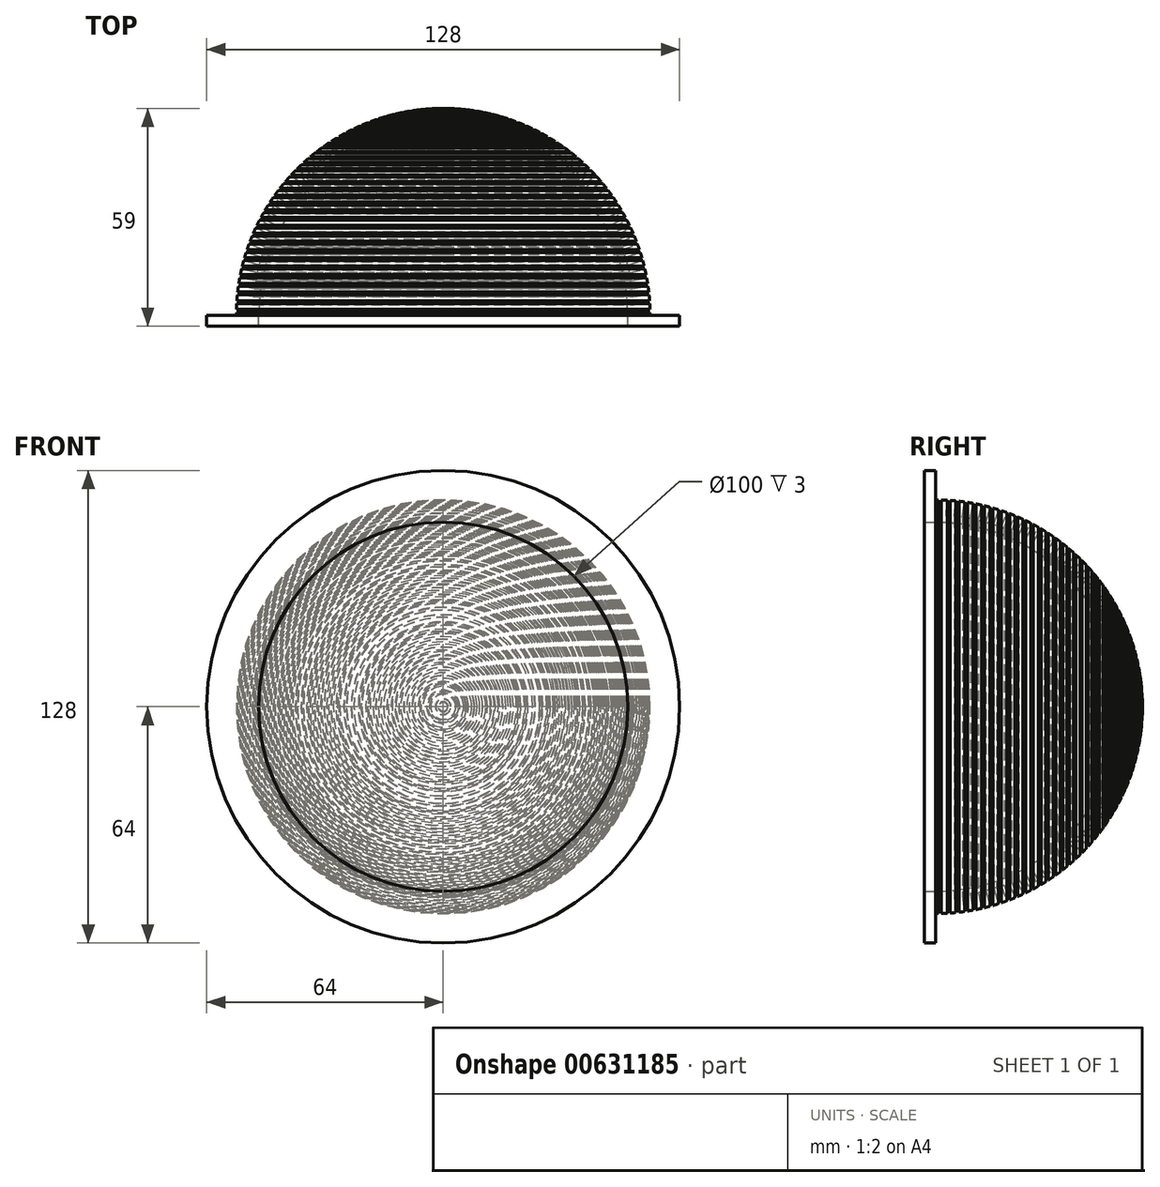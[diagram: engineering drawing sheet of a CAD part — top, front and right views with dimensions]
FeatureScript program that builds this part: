
annotation { "Feature Type Name" : "Feature", "Feature Type Description" : "" }
export const myFeature = defineFeature(function(context is Context, id is Id, definition is map)
    precondition{}
    {
        {
            var Q0;
            Q0=qCreatedBy(makeId("Right.planeOp"),FACE);
            var sketch = newSketch(context, id + "F0", { "sketchPlane" : qUnion([Q0])});
            skArc(sketch, "E0", {"start": v(0, 50) * mm, "mid": v(50, 0) * mm, "end": v(0, -50) * mm});
            skArc(sketch, "E1", {"start": v(0, 56) * mm, "mid": v(56, 0) * mm, "end": v(0, -56) * mm});
            skLineSegment(sketch, "E2", {"start": v(0, 50) * mm, "end": v(0, 56) * mm});
            skLineSegment(sketch, "E3", {"start": v(0, -50) * mm, "end": v(0, -56) * mm});
            skPoint(sketch, "E4", {"position": v(56, 0) * mm});
            skPoint(sketch, "E5", {"position": v(0, 56) * mm});
            skArc(sketch, "E6", {"start": v(0, 51.7) * mm, "mid": v(36.56, 36.56) * mm, "end": v(51.7, 0) * mm, "construction": true});
            skPoint(sketch, "E7", {"position": v(1.1, 51.69) * mm});
            skLineSegment(sketch, "E8", {"start": v(1.1, 51.69) * mm, "end": v(0.7, 51.7) * mm});
            skLineSegment(sketch, "E9", {"start": v(0.7, 51.7) * mm, "end": v(0.83, 57.63) * mm});
            skLineSegment(sketch, "E10", {"start": v(0.83, 57.63) * mm, "end": v(1.63, 57.62) * mm});
            skLineSegment(sketch, "E11", {"start": v(1.63, 57.62) * mm, "end": v(1.5, 51.68) * mm});
            skLineSegment(sketch, "E12", {"start": v(1.5, 51.68) * mm, "end": v(1.1, 51.69) * mm});
            skLineSegment(sketch, "E13.1.0", {"start": v(2.88, 51.62) * mm, "end": v(3.26, 57.55) * mm});
            skPoint(sketch, "E13.1.1", {"position": v(3.28, 51.6) * mm});
            skPoint(sketch, "E13.1.2", {"position": v(2.36, 55.95) * mm});
            skLineSegment(sketch, "E13.1.3", {"start": v(4.05, 57.5) * mm, "end": v(3.68, 51.57) * mm});
            skLineSegment(sketch, "E13.1.4", {"start": v(3.26, 57.55) * mm, "end": v(4.05, 57.5) * mm});
            skLineSegment(sketch, "E13.1.5", {"start": v(3.28, 51.6) * mm, "end": v(2.88, 51.62) * mm});
            skLineSegment(sketch, "E13.1.6", {"start": v(3.68, 51.57) * mm, "end": v(3.28, 51.6) * mm});
            skLineSegment(sketch, "E13.2.0", {"start": v(5.05, 51.45) * mm, "end": v(5.68, 57.36) * mm});
            skPoint(sketch, "E13.2.1", {"position": v(5.45, 51.41) * mm});
            skPoint(sketch, "E13.2.2", {"position": v(4.72, 55.8) * mm});
            skLineSegment(sketch, "E13.2.3", {"start": v(6.48, 57.27) * mm, "end": v(5.85, 51.37) * mm});
            skLineSegment(sketch, "E13.2.4", {"start": v(5.68, 57.36) * mm, "end": v(6.48, 57.27) * mm});
            skLineSegment(sketch, "E13.2.5", {"start": v(5.45, 51.41) * mm, "end": v(5.05, 51.45) * mm});
            skLineSegment(sketch, "E13.2.6", {"start": v(5.85, 51.37) * mm, "end": v(5.45, 51.41) * mm});
            skLineSegment(sketch, "E13.anchor1", {"start": v(0, 0) * mm, "end": v(0.7, 51.7) * mm, "construction": true});
            skLineSegment(sketch, "E13.anchor2", {"start": v(0, 0) * mm, "end": v(51.66, 2) * mm, "construction": true});
            skLineSegment(sketch, "E14.1.3.0", {"start": v(7.22, 51.2) * mm, "end": v(8.1, 57.07) * mm});
            skPoint(sketch, "E14.3.3.0", {"position": v(7.61, 51.14) * mm});
            skPoint(sketch, "E14.4.3.0", {"position": v(7.07, 55.55) * mm});
            skLineSegment(sketch, "E14.5.3.0", {"start": v(8.88, 56.95) * mm, "end": v(8, 51.08) * mm});
            skLineSegment(sketch, "E14.8.3.0", {"start": v(8.1, 57.07) * mm, "end": v(8.88, 56.95) * mm});
            skLineSegment(sketch, "E14.11.3.0", {"start": v(7.61, 51.14) * mm, "end": v(7.22, 51.2) * mm});
            skLineSegment(sketch, "E14.14.3.0", {"start": v(8, 51.08) * mm, "end": v(7.61, 51.14) * mm});
            skLineSegment(sketch, "E14.1.4.0", {"start": v(9.37, 50.85) * mm, "end": v(10.5, 56.68) * mm});
            skPoint(sketch, "E14.3.4.0", {"position": v(9.76, 50.77) * mm});
            skPoint(sketch, "E14.4.4.0", {"position": v(9.4, 55.2) * mm});
            skLineSegment(sketch, "E14.5.4.0", {"start": v(11.28, 56.53) * mm, "end": v(10.16, 50.7) * mm});
            skLineSegment(sketch, "E14.8.4.0", {"start": v(10.5, 56.68) * mm, "end": v(11.28, 56.53) * mm});
            skLineSegment(sketch, "E14.11.4.0", {"start": v(9.76, 50.77) * mm, "end": v(9.37, 50.85) * mm});
            skLineSegment(sketch, "E14.14.4.0", {"start": v(10.16, 50.7) * mm, "end": v(9.76, 50.77) * mm});
            skLineSegment(sketch, "E14.1.5.0", {"start": v(11.5, 50.4) * mm, "end": v(12.87, 56.18) * mm});
            skPoint(sketch, "E14.3.5.0", {"position": v(11.9, 50.31) * mm});
            skPoint(sketch, "E14.4.5.0", {"position": v(11.72, 54.76) * mm});
            skLineSegment(sketch, "E14.5.5.0", {"start": v(13.65, 56) * mm, "end": v(12.28, 50.22) * mm});
            skLineSegment(sketch, "E14.8.5.0", {"start": v(12.87, 56.18) * mm, "end": v(13.65, 56) * mm});
            skLineSegment(sketch, "E14.11.5.0", {"start": v(11.9, 50.31) * mm, "end": v(11.5, 50.4) * mm});
            skLineSegment(sketch, "E14.14.5.0", {"start": v(12.28, 50.22) * mm, "end": v(11.9, 50.31) * mm});
            skLineSegment(sketch, "E14.1.6.0", {"start": v(13.62, 49.87) * mm, "end": v(15.23, 55.6) * mm});
            skPoint(sketch, "E14.3.6.0", {"position": v(14, 49.77) * mm});
            skPoint(sketch, "E14.4.6.0", {"position": v(14.02, 54.22) * mm});
            skLineSegment(sketch, "E14.5.6.0", {"start": v(16, 55.37) * mm, "end": v(14.4, 49.66) * mm});
            skLineSegment(sketch, "E14.8.6.0", {"start": v(15.23, 55.6) * mm, "end": v(16, 55.37) * mm});
            skLineSegment(sketch, "E14.11.6.0", {"start": v(14, 49.77) * mm, "end": v(13.62, 49.87) * mm});
            skLineSegment(sketch, "E14.14.6.0", {"start": v(14.4, 49.66) * mm, "end": v(14, 49.77) * mm});
            skLineSegment(sketch, "E14.1.7.0", {"start": v(15.71, 49.26) * mm, "end": v(17.56, 54.9) * mm});
            skPoint(sketch, "E14.3.7.0", {"position": v(16.1, 49.13) * mm});
            skPoint(sketch, "E14.4.7.0", {"position": v(16.3, 53.58) * mm});
            skLineSegment(sketch, "E14.5.7.0", {"start": v(18.32, 54.65) * mm, "end": v(16.47, 49) * mm});
            skLineSegment(sketch, "E14.8.7.0", {"start": v(17.56, 54.9) * mm, "end": v(18.32, 54.65) * mm});
            skLineSegment(sketch, "E14.11.7.0", {"start": v(16.1, 49.13) * mm, "end": v(15.71, 49.26) * mm});
            skLineSegment(sketch, "E14.14.7.0", {"start": v(16.47, 49) * mm, "end": v(16.1, 49.13) * mm});
            skLineSegment(sketch, "E14.1.8.0", {"start": v(17.78, 48.55) * mm, "end": v(19.86, 54.11) * mm});
            skPoint(sketch, "E14.3.8.0", {"position": v(18.15, 48.4) * mm});
            skPoint(sketch, "E14.4.8.0", {"position": v(18.54, 52.84) * mm});
            skLineSegment(sketch, "E14.5.8.0", {"start": v(20.6, 53.83) * mm, "end": v(18.52, 48.27) * mm});
            skLineSegment(sketch, "E14.8.8.0", {"start": v(19.86, 54.11) * mm, "end": v(20.6, 53.83) * mm});
            skLineSegment(sketch, "E14.11.8.0", {"start": v(18.15, 48.4) * mm, "end": v(17.78, 48.55) * mm});
            skLineSegment(sketch, "E14.14.8.0", {"start": v(18.52, 48.27) * mm, "end": v(18.15, 48.4) * mm});
            skLineSegment(sketch, "E14.1.9.0", {"start": v(19.8, 47.76) * mm, "end": v(22.12, 53.22) * mm});
            skPoint(sketch, "E14.3.9.0", {"position": v(20.18, 47.6) * mm});
            skPoint(sketch, "E14.4.9.0", {"position": v(20.75, 52.01) * mm});
            skLineSegment(sketch, "E14.5.9.0", {"start": v(22.86, 52.91) * mm, "end": v(20.54, 47.44) * mm});
            skLineSegment(sketch, "E14.8.9.0", {"start": v(22.12, 53.22) * mm, "end": v(22.86, 52.91) * mm});
            skLineSegment(sketch, "E14.11.9.0", {"start": v(20.18, 47.6) * mm, "end": v(19.8, 47.76) * mm});
            skLineSegment(sketch, "E14.14.9.0", {"start": v(20.54, 47.44) * mm, "end": v(20.18, 47.6) * mm});
            skLineSegment(sketch, "E14.1.10.0", {"start": v(21.8, 46.88) * mm, "end": v(24.35, 52.24) * mm});
            skPoint(sketch, "E14.3.10.0", {"position": v(22.16, 46.7) * mm});
            skPoint(sketch, "E14.4.10.0", {"position": v(22.93, 51.1) * mm});
            skLineSegment(sketch, "E14.5.10.0", {"start": v(25.07, 51.9) * mm, "end": v(22.53, 46.54) * mm});
            skLineSegment(sketch, "E14.8.10.0", {"start": v(24.35, 52.24) * mm, "end": v(25.07, 51.9) * mm});
            skLineSegment(sketch, "E14.11.10.0", {"start": v(22.16, 46.7) * mm, "end": v(21.8, 46.88) * mm});
            skLineSegment(sketch, "E14.14.10.0", {"start": v(22.53, 46.54) * mm, "end": v(22.16, 46.7) * mm});
            skLineSegment(sketch, "E14.1.11.0", {"start": v(23.76, 45.92) * mm, "end": v(26.53, 51.17) * mm});
            skPoint(sketch, "E14.3.11.0", {"position": v(24.11, 45.73) * mm});
            skPoint(sketch, "E14.4.11.0", {"position": v(25.06, 50.08) * mm});
            skLineSegment(sketch, "E14.5.11.0", {"start": v(27.24, 50.8) * mm, "end": v(24.47, 45.55) * mm});
            skLineSegment(sketch, "E14.8.11.0", {"start": v(26.53, 51.17) * mm, "end": v(27.24, 50.8) * mm});
            skLineSegment(sketch, "E14.11.11.0", {"start": v(24.11, 45.73) * mm, "end": v(23.76, 45.92) * mm});
            skLineSegment(sketch, "E14.14.11.0", {"start": v(24.47, 45.55) * mm, "end": v(24.11, 45.73) * mm});
            skLineSegment(sketch, "E14.1.12.0", {"start": v(25.68, 44.88) * mm, "end": v(28.66, 50) * mm});
            skPoint(sketch, "E14.3.12.0", {"position": v(26.02, 44.67) * mm});
            skPoint(sketch, "E14.4.12.0", {"position": v(27.15, 48.98) * mm});
            skLineSegment(sketch, "E14.5.12.0", {"start": v(29.36, 49.6) * mm, "end": v(26.37, 44.47) * mm});
            skLineSegment(sketch, "E14.8.12.0", {"start": v(28.66, 50) * mm, "end": v(29.36, 49.6) * mm});
            skLineSegment(sketch, "E14.11.12.0", {"start": v(26.02, 44.67) * mm, "end": v(25.68, 44.88) * mm});
            skLineSegment(sketch, "E14.14.12.0", {"start": v(26.37, 44.47) * mm, "end": v(26.02, 44.67) * mm});
            skLineSegment(sketch, "E14.1.13.0", {"start": v(27.54, 43.75) * mm, "end": v(30.75, 48.75) * mm});
            skPoint(sketch, "E14.3.13.0", {"position": v(27.88, 43.54) * mm});
            skPoint(sketch, "E14.4.13.0", {"position": v(29.2, 47.8) * mm});
            skLineSegment(sketch, "E14.5.13.0", {"start": v(31.42, 48.32) * mm, "end": v(28.22, 43.32) * mm});
            skLineSegment(sketch, "E14.8.13.0", {"start": v(30.75, 48.75) * mm, "end": v(31.42, 48.32) * mm});
            skLineSegment(sketch, "E14.11.13.0", {"start": v(27.88, 43.54) * mm, "end": v(27.54, 43.75) * mm});
            skLineSegment(sketch, "E14.14.13.0", {"start": v(28.22, 43.32) * mm, "end": v(27.88, 43.54) * mm});
            skLineSegment(sketch, "E14.1.14.0", {"start": v(29.37, 42.55) * mm, "end": v(32.78, 47.41) * mm});
            skPoint(sketch, "E14.3.14.0", {"position": v(29.7, 42.32) * mm});
            skPoint(sketch, "E14.4.14.0", {"position": v(31.18, 46.52) * mm});
            skLineSegment(sketch, "E14.5.14.0", {"start": v(33.43, 46.95) * mm, "end": v(30.02, 42.1) * mm});
            skLineSegment(sketch, "E14.8.14.0", {"start": v(32.78, 47.41) * mm, "end": v(33.43, 46.95) * mm});
            skLineSegment(sketch, "E14.11.14.0", {"start": v(29.7, 42.32) * mm, "end": v(29.37, 42.55) * mm});
            skLineSegment(sketch, "E14.14.14.0", {"start": v(30.02, 42.1) * mm, "end": v(29.7, 42.32) * mm});
            skLineSegment(sketch, "E15.1.15.0", {"start": v(31.13, 41.28) * mm, "end": v(34.75, 45.99) * mm});
            skPoint(sketch, "E15.3.15.0", {"position": v(31.45, 41.03) * mm});
            skPoint(sketch, "E15.4.15.0", {"position": v(33.11, 45.16) * mm});
            skLineSegment(sketch, "E15.5.15.0", {"start": v(35.38, 45.5) * mm, "end": v(31.77, 40.8) * mm});
            skLineSegment(sketch, "E15.8.15.0", {"start": v(34.75, 45.99) * mm, "end": v(35.38, 45.5) * mm});
            skLineSegment(sketch, "E15.11.15.0", {"start": v(31.45, 41.03) * mm, "end": v(31.13, 41.28) * mm});
            skLineSegment(sketch, "E15.14.15.0", {"start": v(31.77, 40.8) * mm, "end": v(31.45, 41.03) * mm});
            skLineSegment(sketch, "E15.1.16.0", {"start": v(32.85, 39.93) * mm, "end": v(36.65, 44.48) * mm});
            skPoint(sketch, "E15.3.16.0", {"position": v(33.15, 39.67) * mm});
            skPoint(sketch, "E15.4.16.0", {"position": v(34.99, 43.72) * mm});
            skLineSegment(sketch, "E15.5.16.0", {"start": v(37.27, 43.97) * mm, "end": v(33.46, 39.41) * mm});
            skLineSegment(sketch, "E15.8.16.0", {"start": v(36.65, 44.48) * mm, "end": v(37.27, 43.97) * mm});
            skLineSegment(sketch, "E15.11.16.0", {"start": v(33.15, 39.67) * mm, "end": v(32.85, 39.93) * mm});
            skLineSegment(sketch, "E15.14.16.0", {"start": v(33.46, 39.41) * mm, "end": v(33.15, 39.67) * mm});
            skLineSegment(sketch, "E15.1.17.0", {"start": v(34.5, 38.5) * mm, "end": v(38.5, 42.9) * mm});
            skPoint(sketch, "E15.3.17.0", {"position": v(34.8, 38.24) * mm});
            skPoint(sketch, "E15.4.17.0", {"position": v(36.8, 42.21) * mm});
            skLineSegment(sketch, "E15.5.17.0", {"start": v(39.09, 42.36) * mm, "end": v(35.1, 37.97) * mm});
            skLineSegment(sketch, "E15.8.17.0", {"start": v(38.5, 42.9) * mm, "end": v(39.09, 42.36) * mm});
            skLineSegment(sketch, "E15.11.17.0", {"start": v(34.8, 38.24) * mm, "end": v(34.5, 38.5) * mm});
            skLineSegment(sketch, "E15.14.17.0", {"start": v(35.1, 37.97) * mm, "end": v(34.8, 38.24) * mm});
            skLineSegment(sketch, "E15.1.18.0", {"start": v(36.1, 37.02) * mm, "end": v(40.27, 41.24) * mm});
            skPoint(sketch, "E15.3.18.0", {"position": v(36.38, 36.74) * mm});
            skPoint(sketch, "E15.4.18.0", {"position": v(38.55, 40.62) * mm});
            skLineSegment(sketch, "E15.5.18.0", {"start": v(40.84, 40.67) * mm, "end": v(36.66, 36.45) * mm});
            skLineSegment(sketch, "E15.8.18.0", {"start": v(40.27, 41.24) * mm, "end": v(40.84, 40.67) * mm});
            skLineSegment(sketch, "E15.11.18.0", {"start": v(36.38, 36.74) * mm, "end": v(36.1, 37.02) * mm});
            skLineSegment(sketch, "E15.14.18.0", {"start": v(36.66, 36.45) * mm, "end": v(36.38, 36.74) * mm});
            skLineSegment(sketch, "E15.1.19.0", {"start": v(37.62, 35.46) * mm, "end": v(41.97, 39.5) * mm});
            skPoint(sketch, "E15.3.19.0", {"position": v(37.9, 35.17) * mm});
            skPoint(sketch, "E15.4.19.0", {"position": v(40.23, 38.96) * mm});
            skLineSegment(sketch, "E15.5.19.0", {"start": v(42.52, 38.92) * mm, "end": v(38.17, 34.88) * mm});
            skLineSegment(sketch, "E15.8.19.0", {"start": v(41.97, 39.5) * mm, "end": v(42.52, 38.92) * mm});
            skLineSegment(sketch, "E15.11.19.0", {"start": v(37.9, 35.17) * mm, "end": v(37.62, 35.46) * mm});
            skLineSegment(sketch, "E15.14.19.0", {"start": v(38.17, 34.88) * mm, "end": v(37.9, 35.17) * mm});
            skLineSegment(sketch, "E16.1.20.0", {"start": v(39.08, 33.84) * mm, "end": v(43.6, 37.7) * mm});
            skPoint(sketch, "E16.3.20.0", {"position": v(39.34, 33.54) * mm});
            skPoint(sketch, "E16.4.20.0", {"position": v(41.83, 37.23) * mm});
            skLineSegment(sketch, "E16.5.20.0", {"start": v(44.12, 37.09) * mm, "end": v(39.6, 33.24) * mm});
            skLineSegment(sketch, "E16.8.20.0", {"start": v(43.6, 37.7) * mm, "end": v(44.12, 37.09) * mm});
            skLineSegment(sketch, "E16.11.20.0", {"start": v(39.34, 33.54) * mm, "end": v(39.08, 33.84) * mm});
            skLineSegment(sketch, "E16.14.20.0", {"start": v(39.6, 33.24) * mm, "end": v(39.34, 33.54) * mm});
            skLineSegment(sketch, "E16.1.21.0", {"start": v(40.48, 32.17) * mm, "end": v(45.15, 35.83) * mm});
            skPoint(sketch, "E16.3.21.0", {"position": v(40.72, 31.85) * mm});
            skPoint(sketch, "E16.4.21.0", {"position": v(43.37, 35.43) * mm});
            skLineSegment(sketch, "E16.5.21.0", {"start": v(45.65, 35.2) * mm, "end": v(40.97, 31.54) * mm});
            skLineSegment(sketch, "E16.8.21.0", {"start": v(45.15, 35.83) * mm, "end": v(45.65, 35.2) * mm});
            skLineSegment(sketch, "E16.11.21.0", {"start": v(40.72, 31.85) * mm, "end": v(40.48, 32.17) * mm});
            skLineSegment(sketch, "E16.14.21.0", {"start": v(40.97, 31.54) * mm, "end": v(40.72, 31.85) * mm});
            skLineSegment(sketch, "E16.1.22.0", {"start": v(41.8, 30.43) * mm, "end": v(46.62, 33.89) * mm});
            skPoint(sketch, "E16.3.22.0", {"position": v(42.03, 30.1) * mm});
            skPoint(sketch, "E16.4.22.0", {"position": v(44.82, 33.57) * mm});
            skLineSegment(sketch, "E16.5.22.0", {"start": v(47.1, 33.24) * mm, "end": v(42.26, 29.78) * mm});
            skLineSegment(sketch, "E16.8.22.0", {"start": v(46.62, 33.89) * mm, "end": v(47.1, 33.24) * mm});
            skLineSegment(sketch, "E16.11.22.0", {"start": v(42.03, 30.1) * mm, "end": v(41.8, 30.43) * mm});
            skLineSegment(sketch, "E16.14.22.0", {"start": v(42.26, 29.78) * mm, "end": v(42.03, 30.1) * mm});
            skLineSegment(sketch, "E16.1.23.0", {"start": v(43.04, 28.64) * mm, "end": v(48.01, 31.9) * mm});
            skPoint(sketch, "E16.3.23.0", {"position": v(43.26, 28.3) * mm});
            skPoint(sketch, "E16.4.23.0", {"position": v(46.2, 31.65) * mm});
            skLineSegment(sketch, "E16.5.23.0", {"start": v(48.45, 31.22) * mm, "end": v(43.48, 27.97) * mm});
            skLineSegment(sketch, "E16.8.23.0", {"start": v(48.01, 31.9) * mm, "end": v(48.45, 31.22) * mm});
            skLineSegment(sketch, "E16.11.23.0", {"start": v(43.26, 28.3) * mm, "end": v(43.04, 28.64) * mm});
            skLineSegment(sketch, "E16.14.23.0", {"start": v(43.48, 27.97) * mm, "end": v(43.26, 28.3) * mm});
            skLineSegment(sketch, "E16.1.24.0", {"start": v(44.21, 26.8) * mm, "end": v(49.31, 29.84) * mm});
            skPoint(sketch, "E16.3.24.0", {"position": v(44.42, 26.46) * mm});
            skPoint(sketch, "E16.4.24.0", {"position": v(47.5, 29.68) * mm});
            skLineSegment(sketch, "E16.5.24.0", {"start": v(49.72, 29.15) * mm, "end": v(44.62, 26.11) * mm});
            skLineSegment(sketch, "E16.8.24.0", {"start": v(49.31, 29.84) * mm, "end": v(49.72, 29.15) * mm});
            skLineSegment(sketch, "E16.11.24.0", {"start": v(44.42, 26.46) * mm, "end": v(44.21, 26.8) * mm});
            skLineSegment(sketch, "E16.14.24.0", {"start": v(44.62, 26.11) * mm, "end": v(44.42, 26.46) * mm});
            skLineSegment(sketch, "E16.1.25.0", {"start": v(45.3, 24.91) * mm, "end": v(50.53, 27.73) * mm});
            skPoint(sketch, "E16.3.25.0", {"position": v(45.5, 24.56) * mm});
            skPoint(sketch, "E16.4.25.0", {"position": v(48.7, 27.65) * mm});
            skLineSegment(sketch, "E16.5.25.0", {"start": v(50.9, 27.03) * mm, "end": v(45.68, 24.2) * mm});
            skLineSegment(sketch, "E16.8.25.0", {"start": v(50.53, 27.73) * mm, "end": v(50.9, 27.03) * mm});
            skLineSegment(sketch, "E16.11.25.0", {"start": v(45.5, 24.56) * mm, "end": v(45.3, 24.91) * mm});
            skLineSegment(sketch, "E16.14.25.0", {"start": v(45.68, 24.2) * mm, "end": v(45.5, 24.56) * mm});
            skLineSegment(sketch, "E16.1.26.0", {"start": v(46.31, 22.98) * mm, "end": v(51.65, 25.58) * mm});
            skPoint(sketch, "E16.3.26.0", {"position": v(46.49, 22.62) * mm});
            skPoint(sketch, "E16.4.26.0", {"position": v(49.82, 25.57) * mm});
            skLineSegment(sketch, "E16.5.26.0", {"start": v(52, 24.86) * mm, "end": v(46.66, 22.26) * mm});
            skLineSegment(sketch, "E16.8.26.0", {"start": v(51.65, 25.58) * mm, "end": v(52, 24.86) * mm});
            skLineSegment(sketch, "E16.11.26.0", {"start": v(46.49, 22.62) * mm, "end": v(46.31, 22.98) * mm});
            skLineSegment(sketch, "E16.14.26.0", {"start": v(46.66, 22.26) * mm, "end": v(46.49, 22.62) * mm});
            skLineSegment(sketch, "E16.1.27.0", {"start": v(47.24, 21) * mm, "end": v(52.69, 23.38) * mm});
            skPoint(sketch, "E16.3.27.0", {"position": v(47.4, 20.64) * mm});
            skPoint(sketch, "E16.4.27.0", {"position": v(50.86, 23.44) * mm});
            skLineSegment(sketch, "E16.5.27.0", {"start": v(53, 22.65) * mm, "end": v(47.56, 20.27) * mm});
            skLineSegment(sketch, "E16.8.27.0", {"start": v(52.69, 23.38) * mm, "end": v(53, 22.65) * mm});
            skLineSegment(sketch, "E16.11.27.0", {"start": v(47.4, 20.64) * mm, "end": v(47.24, 21) * mm});
            skLineSegment(sketch, "E16.14.27.0", {"start": v(47.56, 20.27) * mm, "end": v(47.4, 20.64) * mm});
            skLineSegment(sketch, "E16.1.28.0", {"start": v(48.08, 19) * mm, "end": v(53.62, 21.14) * mm});
            skPoint(sketch, "E16.3.28.0", {"position": v(48.23, 18.62) * mm});
            skPoint(sketch, "E16.4.28.0", {"position": v(51.8, 21.28) * mm});
            skLineSegment(sketch, "E16.5.28.0", {"start": v(53.91, 20.39) * mm, "end": v(48.37, 18.25) * mm});
            skLineSegment(sketch, "E16.8.28.0", {"start": v(53.62, 21.14) * mm, "end": v(53.91, 20.39) * mm});
            skLineSegment(sketch, "E16.11.28.0", {"start": v(48.23, 18.62) * mm, "end": v(48.08, 19) * mm});
            skLineSegment(sketch, "E16.14.28.0", {"start": v(48.37, 18.25) * mm, "end": v(48.23, 18.62) * mm});
            skLineSegment(sketch, "E16.1.29.0", {"start": v(48.84, 16.95) * mm, "end": v(54.47, 18.86) * mm});
            skPoint(sketch, "E16.3.29.0", {"position": v(48.97, 16.57) * mm});
            skPoint(sketch, "E16.4.29.0", {"position": v(52.65, 19.08) * mm});
            skLineSegment(sketch, "E16.5.29.0", {"start": v(54.72, 18.1) * mm, "end": v(49.1, 16.2) * mm});
            skLineSegment(sketch, "E16.8.29.0", {"start": v(54.47, 18.86) * mm, "end": v(54.72, 18.1) * mm});
            skLineSegment(sketch, "E16.11.29.0", {"start": v(48.97, 16.57) * mm, "end": v(48.84, 16.95) * mm});
            skLineSegment(sketch, "E16.14.29.0", {"start": v(49.1, 16.2) * mm, "end": v(48.97, 16.57) * mm});
            skLineSegment(sketch, "E17.1.30.0", {"start": v(49.51, 14.88) * mm, "end": v(55.21, 16.54) * mm});
            skPoint(sketch, "E17.3.30.0", {"position": v(49.63, 14.5) * mm});
            skPoint(sketch, "E17.4.30.0", {"position": v(53.4, 16.84) * mm});
            skLineSegment(sketch, "E17.5.30.0", {"start": v(55.44, 15.77) * mm, "end": v(49.74, 14.1) * mm});
            skLineSegment(sketch, "E17.8.30.0", {"start": v(55.21, 16.54) * mm, "end": v(55.44, 15.77) * mm});
            skLineSegment(sketch, "E17.11.30.0", {"start": v(49.63, 14.5) * mm, "end": v(49.51, 14.88) * mm});
            skLineSegment(sketch, "E17.14.30.0", {"start": v(49.74, 14.1) * mm, "end": v(49.63, 14.5) * mm});
            skLineSegment(sketch, "E17.1.31.0", {"start": v(50.1, 12.78) * mm, "end": v(55.86, 14.2) * mm});
            skPoint(sketch, "E17.3.31.0", {"position": v(50.2, 12.39) * mm});
            skPoint(sketch, "E17.4.31.0", {"position": v(54.07, 14.57) * mm});
            skLineSegment(sketch, "E17.5.31.0", {"start": v(56.06, 13.42) * mm, "end": v(50.29, 12) * mm});
            skLineSegment(sketch, "E17.8.31.0", {"start": v(55.86, 14.2) * mm, "end": v(56.06, 13.42) * mm});
            skLineSegment(sketch, "E17.11.31.0", {"start": v(50.2, 12.39) * mm, "end": v(50.1, 12.78) * mm});
            skLineSegment(sketch, "E17.14.31.0", {"start": v(50.29, 12) * mm, "end": v(50.2, 12.39) * mm});
            skLineSegment(sketch, "E18.1.32.0", {"start": v(50.6, 10.65) * mm, "end": v(56.41, 11.83) * mm});
            skPoint(sketch, "E18.3.32.0", {"position": v(50.67, 10.26) * mm});
            skPoint(sketch, "E18.4.32.0", {"position": v(54.64, 12.28) * mm});
            skLineSegment(sketch, "E18.5.32.0", {"start": v(56.57, 11.05) * mm, "end": v(50.75, 9.87) * mm});
            skLineSegment(sketch, "E18.8.32.0", {"start": v(56.41, 11.83) * mm, "end": v(56.57, 11.05) * mm});
            skLineSegment(sketch, "E18.11.32.0", {"start": v(50.67, 10.26) * mm, "end": v(50.6, 10.65) * mm});
            skLineSegment(sketch, "E18.14.32.0", {"start": v(50.75, 9.87) * mm, "end": v(50.67, 10.26) * mm});
            skLineSegment(sketch, "E18.1.33.0", {"start": v(51, 8.51) * mm, "end": v(56.86, 9.44) * mm});
            skPoint(sketch, "E18.3.33.0", {"position": v(51.06, 8.12) * mm});
            skPoint(sketch, "E18.4.33.0", {"position": v(55.1, 9.96) * mm});
            skLineSegment(sketch, "E18.5.33.0", {"start": v(56.99, 8.65) * mm, "end": v(51.12, 7.72) * mm});
            skLineSegment(sketch, "E18.8.33.0", {"start": v(56.86, 9.44) * mm, "end": v(56.99, 8.65) * mm});
            skLineSegment(sketch, "E18.11.33.0", {"start": v(51.06, 8.12) * mm, "end": v(51, 8.51) * mm});
            skLineSegment(sketch, "E18.14.33.0", {"start": v(51.12, 7.72) * mm, "end": v(51.06, 8.12) * mm});
            skLineSegment(sketch, "E18.1.34.0", {"start": v(51.3, 6.35) * mm, "end": v(57.2, 7.04) * mm});
            skPoint(sketch, "E18.3.34.0", {"position": v(51.36, 5.96) * mm});
            skPoint(sketch, "E18.4.34.0", {"position": v(55.48, 7.63) * mm});
            skLineSegment(sketch, "E18.5.34.0", {"start": v(57.3, 6.24) * mm, "end": v(51.4, 5.56) * mm});
            skLineSegment(sketch, "E18.8.34.0", {"start": v(57.2, 7.04) * mm, "end": v(57.3, 6.24) * mm});
            skLineSegment(sketch, "E18.11.34.0", {"start": v(51.36, 5.96) * mm, "end": v(51.3, 6.35) * mm});
            skLineSegment(sketch, "E18.14.34.0", {"start": v(51.4, 5.56) * mm, "end": v(51.36, 5.96) * mm});
            skLineSegment(sketch, "E19.1.35.0", {"start": v(51.53, 4.18) * mm, "end": v(57.45, 4.62) * mm});
            skPoint(sketch, "E19.3.35.0", {"position": v(51.56, 3.78) * mm});
            skPoint(sketch, "E19.4.35.0", {"position": v(55.75, 5.29) * mm});
            skLineSegment(sketch, "E19.5.35.0", {"start": v(57.51, 3.82) * mm, "end": v(51.6, 3.39) * mm});
            skLineSegment(sketch, "E19.8.35.0", {"start": v(57.45, 4.62) * mm, "end": v(57.51, 3.82) * mm});
            skLineSegment(sketch, "E19.11.35.0", {"start": v(51.56, 3.78) * mm, "end": v(51.53, 4.18) * mm});
            skLineSegment(sketch, "E19.14.35.0", {"start": v(51.6, 3.39) * mm, "end": v(51.56, 3.78) * mm});
            skLineSegment(sketch, "E20.1.36.0", {"start": v(51.66, 2) * mm, "end": v(57.6, 2.2) * mm});
            skPoint(sketch, "E20.3.36.0", {"position": v(51.68, 1.6) * mm});
            skPoint(sketch, "E20.4.36.0", {"position": v(55.92, 2.93) * mm});
            skLineSegment(sketch, "E20.5.36.0", {"start": v(57.62, 1.4) * mm, "end": v(51.69, 1.2) * mm});
            skLineSegment(sketch, "E20.8.36.0", {"start": v(57.6, 2.2) * mm, "end": v(57.62, 1.4) * mm});
            skLineSegment(sketch, "E20.11.36.0", {"start": v(51.68, 1.6) * mm, "end": v(51.66, 2) * mm});
            skLineSegment(sketch, "E20.14.36.0", {"start": v(51.69, 1.2) * mm, "end": v(51.68, 1.6) * mm});
            skLineSegment(sketch, "E21", {"start": v(0, 0) * mm, "end": v(-28.83, 0) * mm, "construction": true});
            skLineSegment(sketch, "E22", {"start": v(56, 0) * mm, "end": v(50, 0) * mm});
            skLineSegment(sketch, "E23", {"start": v(0, 50) * mm, "end": v(-3, 50) * mm});
            skLineSegment(sketch, "E24", {"start": v(-3, 50) * mm, "end": v(-3, 64) * mm});
            skLineSegment(sketch, "E25", {"start": v(-3, 64) * mm, "end": v(0, 64) * mm});
            skLineSegment(sketch, "E26", {"start": v(0, 64) * mm, "end": v(0, 56) * mm});
            skSolve(sketch);
        }
        {
            var Q0;
            {var subQ144=sQuery(id+"F0.wireOp",EDGE,"E2");Q0=makeQuery(id+"F0.imprint","IMPRINT",FACE,{"disambiguationData":[TD([[makeQuery(id+"F0.imprint","IMPRINT",EDGE,{"derivedFrom":subQ144}),-1.0]])]});}
            var Q1;
            Q1=makeQuery(id+"F0.imprint","IMPRINT",FACE,{"disambiguationData":[TD([[makeQuery(id+"F0.imprint","IMPRINT",EDGE,{"derivedFrom":sQuery(id+"F0.wireOp",EDGE,"E2")}),1.0]])]});
            var Q2;
            Q2=sQuery(id+"F0.wireOp",EDGE,"E21");
            revolve(context, id + "F1", {"entities" : qUnion([Q0, Q1]), "axis" : qUnion([Q2]), "revolveType" : RevolveType.FULL});
        }
    });
